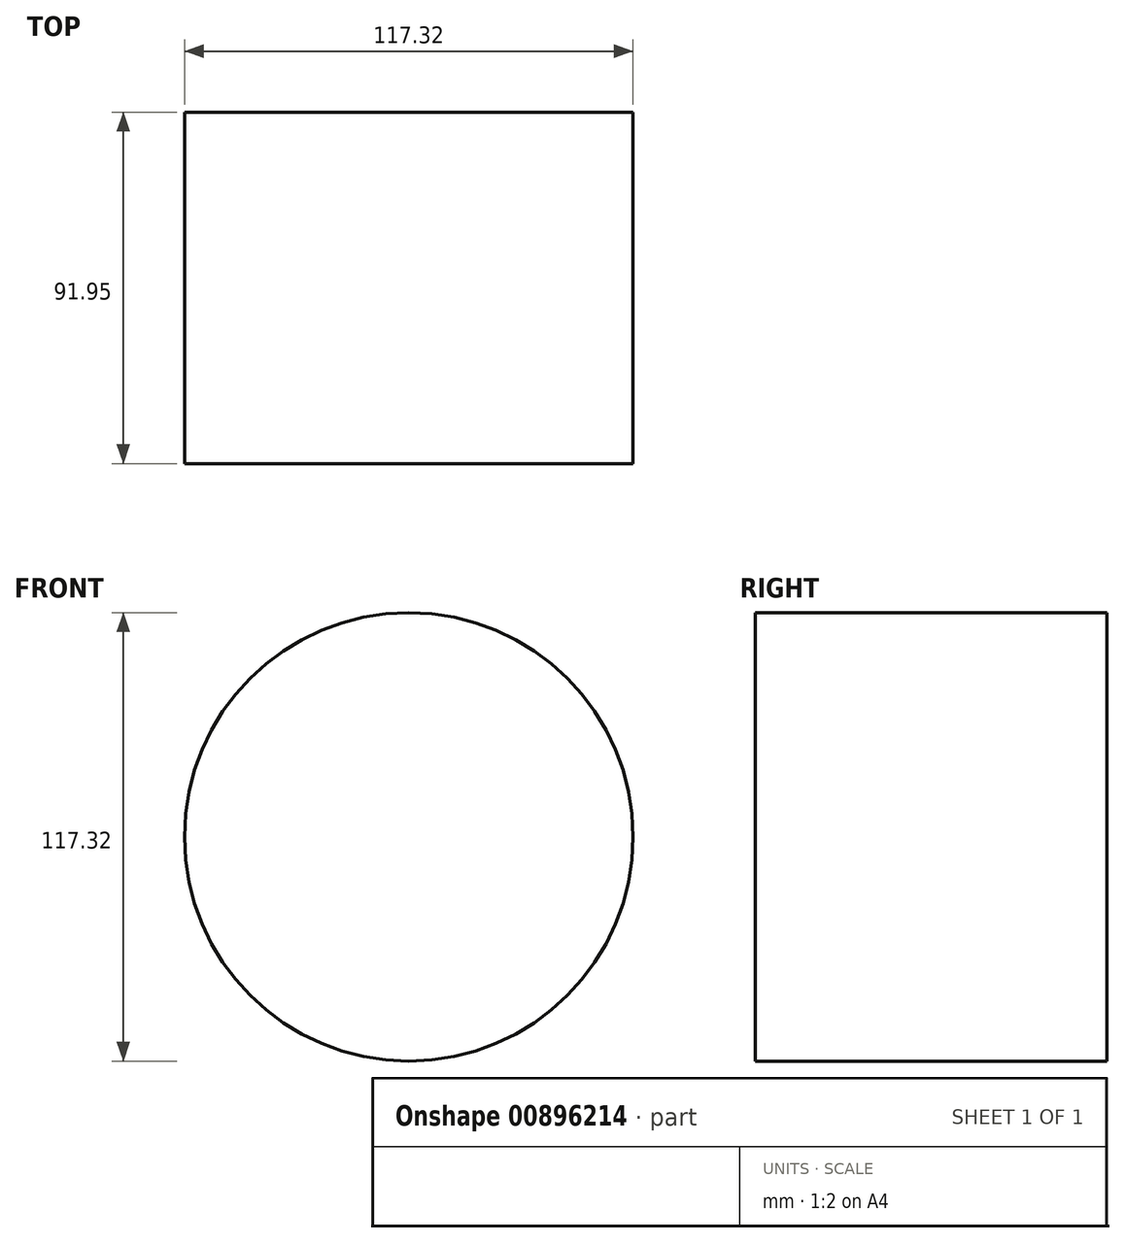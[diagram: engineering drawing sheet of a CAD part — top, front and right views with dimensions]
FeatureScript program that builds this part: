
annotation { "Feature Type Name" : "Feature", "Feature Type Description" : "" }
export const myFeature = defineFeature(function(context is Context, id is Id, definition is map)
    precondition{}
    {
        {
            var Q0;
            Q0=qCreatedBy(makeId("Front.planeOp"),FACE);
            var sketch = newSketch(context, id + "F0", { "sketchPlane" : qUnion([Q0])});
            skCircle(sketch, "E0", {"center": v(0, 0) * mm, "radius": 58.66 * mm});
            skSolve(sketch);
        }
        {
            var Q0;
            Q0 = qSketchRegion(id + "F0", true);
            extrude(context, id + "F1", {"entities" : qUnion([Q0]), "depth" : 91.95 * mm, "offsetDistance" : 25.4 * mm});
        }
    });
